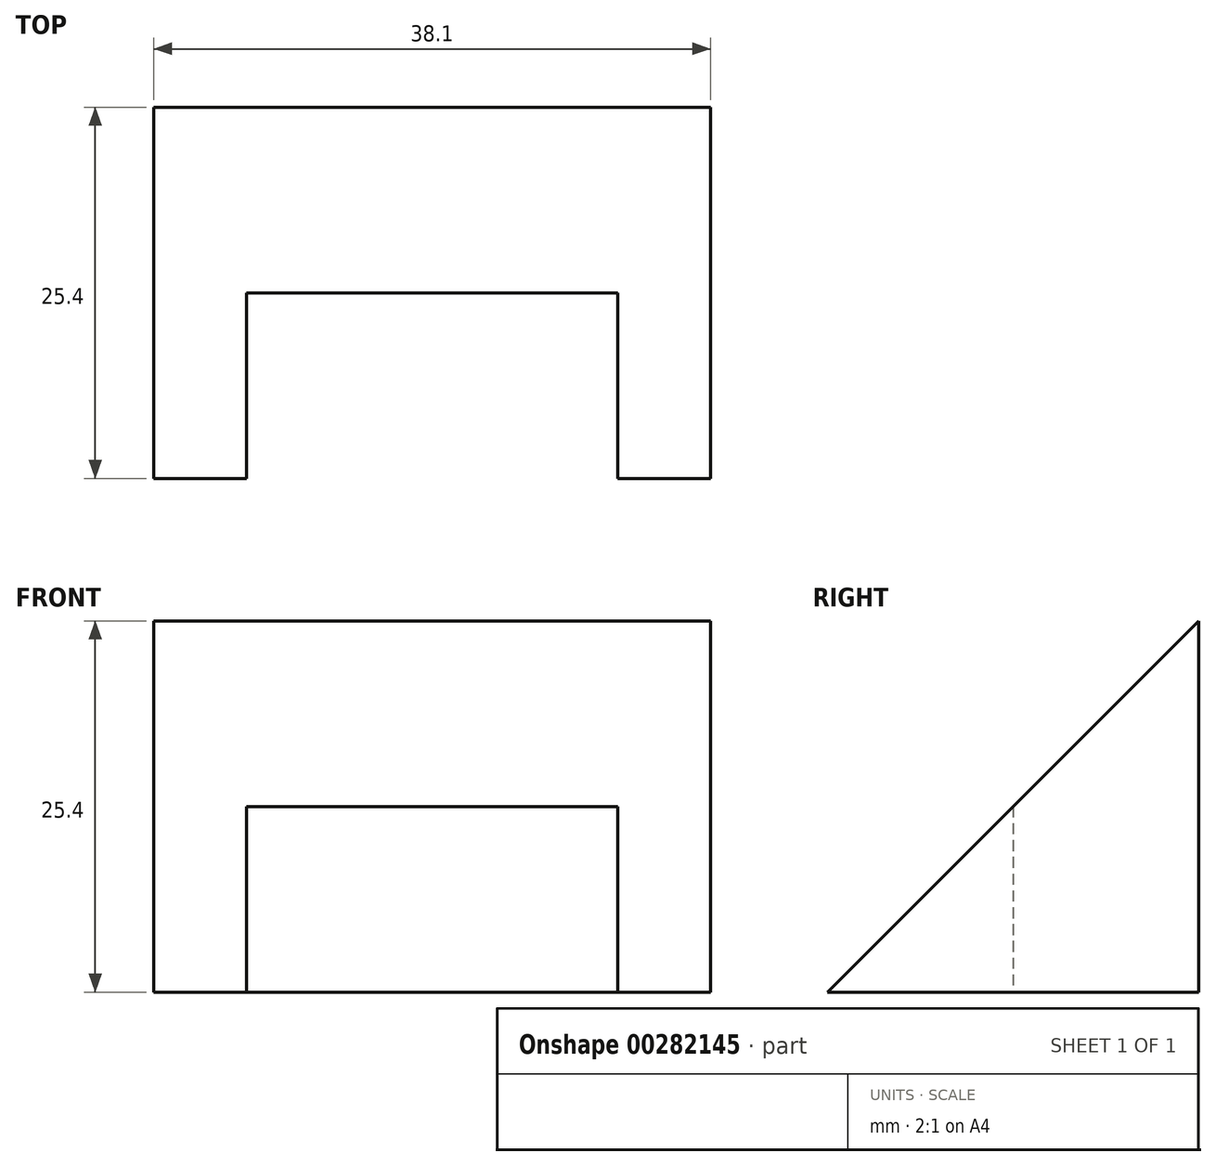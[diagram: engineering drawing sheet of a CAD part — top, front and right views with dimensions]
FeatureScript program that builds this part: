
annotation { "Feature Type Name" : "Feature", "Feature Type Description" : "" }
export const myFeature = defineFeature(function(context is Context, id is Id, definition is map)
    precondition{}
    {
        {
            var Q0;
            Q0=qCreatedBy(makeId("Right.planeOp"),FACE);
            var sketch = newSketch(context, id + "F0", { "sketchPlane" : qUnion([Q0])});
            skLineSegment(sketch, "E0", {"start": v(0, 0) * mm, "end": v(0, 25.4) * mm});
            skLineSegment(sketch, "E1", {"start": v(0, 25.4) * mm, "end": v(-25.4, 0) * mm});
            skLineSegment(sketch, "E2", {"start": v(-25.4, 0) * mm, "end": v(0, 0) * mm});
            skLineSegment(sketch, "E3", {"start": v(-12.7, 12.7) * mm, "end": v(-12.7, 0) * mm});
            skSolve(sketch);
        }
        {
            var Q0;
            {var subQ0=sQuery(id+"F0.wireOp",EDGE,"E0");Q0=makeQuery(id+"F0.imprint","IMPRINT",FACE,{"disambiguationData":[TD([[makeQuery(id+"F0.imprint","IMPRINT",EDGE,{"derivedFrom":subQ0}),1.0]])]});}
            var Q1;
            {var subQ3=sQuery(id+"F0.wireOp",EDGE,"E3");Q1=makeQuery(id+"F0.imprint","IMPRINT",FACE,{"disambiguationData":[TD([[makeQuery(id+"F0.imprint","IMPRINT",EDGE,{"derivedFrom":subQ3}),-1.0]])]});}
            extrude(context, id + "F1", {"entities" : qUnion([Q0, Q1]), "endBound" : BoundingType.SYMMETRIC, "depth" : 38.1 * mm});
        }
        {
            var Q0;
            {var subQ3=sQuery(id+"F0.wireOp",EDGE,"E3");Q0=makeQuery(id+"F0.imprint","IMPRINT",FACE,{"disambiguationData":[TD([[makeQuery(id+"F0.imprint","IMPRINT",EDGE,{"derivedFrom":subQ3}),-1.0]])]});}
            extrude(context, id + "F2", {"entities" : qUnion([Q0]), "operationType" : NewBodyOperationType.REMOVE, "endBound" : BoundingType.SYMMETRIC, "depth" : 25.4 * mm});
        }
    });
